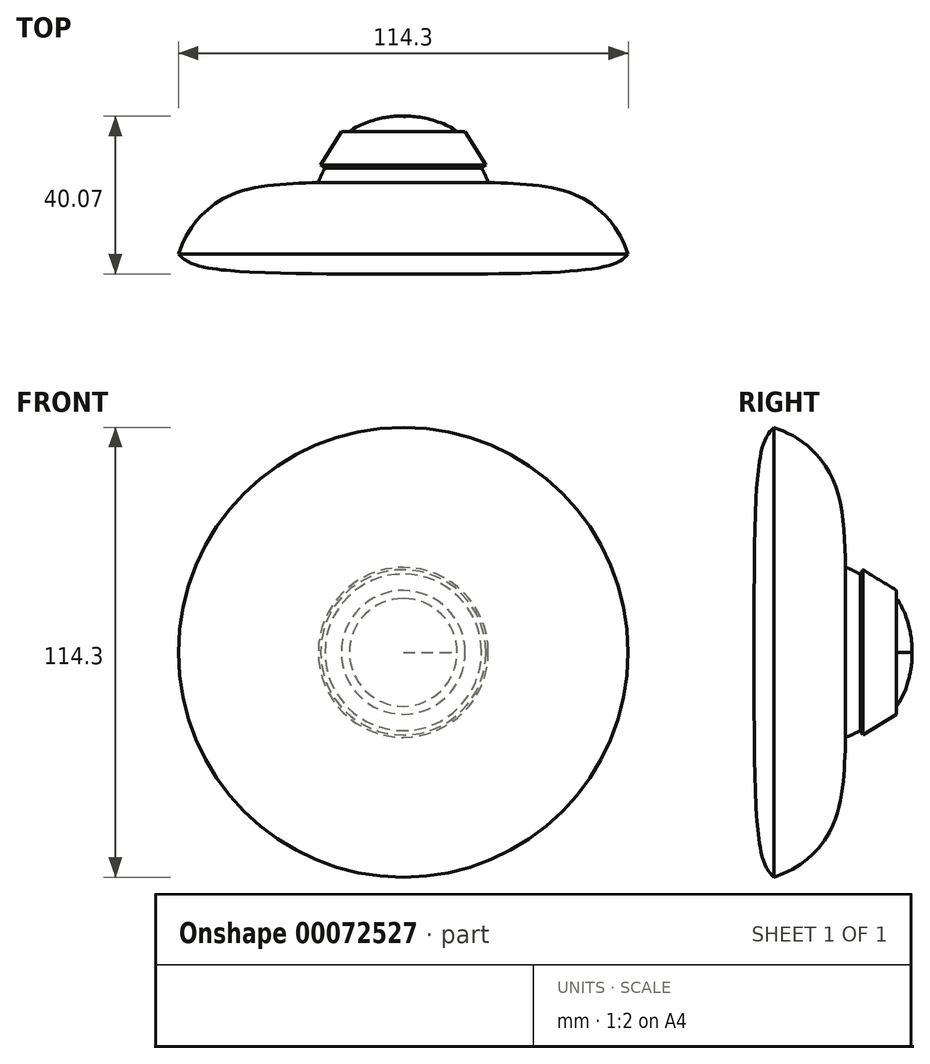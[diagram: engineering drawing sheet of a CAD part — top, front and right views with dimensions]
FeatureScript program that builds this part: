
annotation { "Feature Type Name" : "Feature", "Feature Type Description" : "" }
export const myFeature = defineFeature(function(context is Context, id is Id, definition is map)
    precondition{}
    {
        {
            var Q0;
            Q0=qCreatedBy(makeId("Top.planeOp"),FACE);
            var sketch = newSketch(context, id + "F0", { "sketchPlane" : qUnion([Q0])});
            skFitSpline(sketch, "E0", {"points": [v(0, 34.92) * mm, v(13.7, 31.13) * mm, v(19.62, 22.45) * mm, v(21.58, 18.18) * mm], "startDerivative": vector(22.5, 3.46) * mm, "endDerivative": vector(4.33, -15.1) * mm});
            skFitSpline(sketch, "E1", {"points": [v(21.58, 18.18) * mm, v(43.38, 15.18) * mm, v(53.73, 6.9) * mm, v(57.15, 0) * mm], "startDerivative": vector(56.1, -1.82) * mm, "endDerivative": vector(10.58, -27.2) * mm});
            skFitSpline(sketch, "E2", {"points": [v(57.15, 0) * mm, v(52.53, -2.85) * mm, v(0, -5) * mm], "startDerivative": vector(-12.85, -12.82) * mm, "endDerivative": vector(-88.49, 0.55) * mm});
            skLineSegment(sketch, "E3", {"start": v(0, 34.92) * mm, "end": v(0, -5) * mm});
            skLineSegment(sketch, "E4", {"start": v(13.7, 31.13) * mm, "end": v(15.73, 31.13) * mm});
            skLineSegment(sketch, "E5", {"start": v(15.73, 31.13) * mm, "end": v(20.99, 22.54) * mm});
            skLineSegment(sketch, "E6", {"start": v(20.99, 22.54) * mm, "end": v(19.9, 21.88) * mm});
            skSolve(sketch);
        }
        {
            var Q0;
            {var subQ0=sQuery(id+"F0.wireOp",EDGE,"E4");Q0=makeQuery(id+"F0.imprint","IMPRINT",FACE,{"disambiguationData":[TD([[makeQuery(id+"F0.imprint","IMPRINT",EDGE,{"derivedFrom":subQ0}),-1.0]])]});}
            var Q1;
            {var subQ0=sQuery(id+"F0.wireOp",EDGE,"E1");Q1=makeQuery(id+"F0.imprint","IMPRINT",FACE,{"disambiguationData":[TD([[makeQuery(id+"F0.imprint","IMPRINT",EDGE,{"derivedFrom":subQ0}),-1.0]])]});}
            var Q2;
            Q2=sQuery(id+"F0.wireOp",EDGE,"E3");
            revolve(context, id + "F1", {"entities" : qUnion([Q0, Q1]), "axis" : qUnion([Q2]), "revolveType" : RevolveType.FULL});
        }
    });
